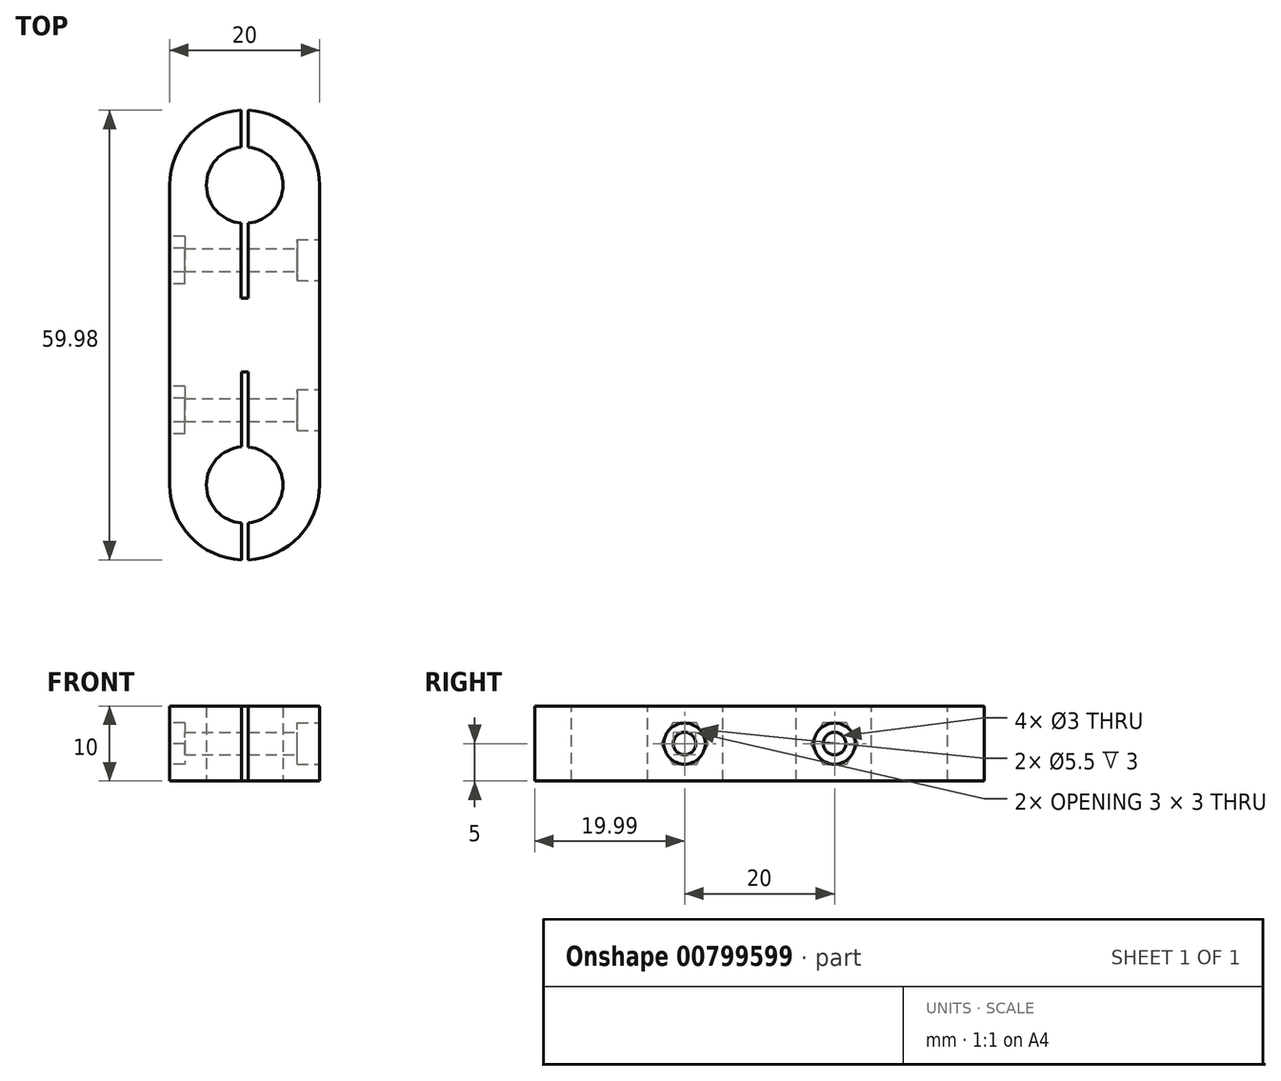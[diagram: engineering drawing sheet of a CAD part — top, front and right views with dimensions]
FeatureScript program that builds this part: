
annotation { "Feature Type Name" : "Feature", "Feature Type Description" : "" }
export const myFeature = defineFeature(function(context is Context, id is Id, definition is map)
    precondition{}
    {
        {
            var Q0;
            Q0=qCreatedBy(makeId("Top.planeOp"),FACE);
            var sketch = newSketch(context, id + "F0", { "sketchPlane" : qUnion([Q0])});
            skCircle(sketch, "E0", {"center": v(0, 0) * mm, "radius": 5.1 * mm});
            skCircle(sketch, "E1", {"center": v(0, 0) * mm, "radius": 10 * mm});
            skPoint(sketch, "E2", {"position": v(0, -40) * mm});
            skCircle(sketch, "E3", {"center": v(0, -40) * mm, "radius": 5.1 * mm});
            skCircle(sketch, "E4", {"center": v(0, -40) * mm, "radius": 10 * mm});
            skLineSegment(sketch, "E5", {"start": v(10, 0) * mm, "end": v(10, -40) * mm});
            skLineSegment(sketch, "E6", {"start": v(-10, 0) * mm, "end": v(-10, -40) * mm});
            skSolve(sketch);
        }
        {
            var Q0;
            Q0=makeQuery(id+"F0.imprint","IMPRINT",FACE,{"disambiguationData":[TD([[makeQuery(id+"F0.imprint","IMPRINT",EDGE,{"derivedFrom":sQuery(id+"F0.wireOp",EDGE,"E0")}),-1.0]])]});
            var Q1;
            {var subQ0=sQuery(id+"F0.wireOp",EDGE,"E5");Q1=makeQuery(id+"F0.imprint","IMPRINT",FACE,{"disambiguationData":[TD([[makeQuery(id+"F0.imprint","IMPRINT",EDGE,{"derivedFrom":subQ0}),-1.0]])]});}
            var Q2;
            Q2=makeQuery(id+"F0.imprint","IMPRINT",FACE,{"disambiguationData":[TD([[makeQuery(id+"F0.imprint","IMPRINT",EDGE,{"derivedFrom":sQuery(id+"F0.wireOp",EDGE,"E3")}),-1.0]])]});
            extrude(context, id + "F1", {"entities" : qUnion([Q0, Q1, Q2]), "depth" : 10 * mm, "offsetDistance" : 25 * mm});
        }
        {
            var Q0;
            Q0=makeQuery(id+"F1.opExtrude","SWEPT_FACE",FACE,{"disambiguationData":[OSD([sQuery(id+"F0.wireOp",EDGE,"E5")])]});
            var sketch = newSketch(context, id + "F2", { "sketchPlane" : qUnion([Q0])});
            skPoint(sketch, "E7", {"position": v(-30, 5) * mm});
            skPoint(sketch, "E8", {"position": v(-10, 5) * mm});
            skCircle(sketch, "E9", {"center": v(-30, 5) * mm, "radius": 1.5 * mm});
            skCircle(sketch, "E10", {"center": v(-10, 5) * mm, "radius": 1.5 * mm});
            skSolve(sketch);
        }
        {
            var Q0;
            Q0=makeQuery(id+"F2.imprint","IMPRINT",FACE,{"disambiguationData":[TD([[makeQuery(id+"F2.imprint","IMPRINT",EDGE,{"derivedFrom":sQuery(id+"F2.wireOp",EDGE,"E9")}),1.0]])]});
            var Q1;
            Q1=makeQuery(id+"F2.imprint","IMPRINT",FACE,{"disambiguationData":[TD([[makeQuery(id+"F2.imprint","IMPRINT",EDGE,{"derivedFrom":sQuery(id+"F2.wireOp",EDGE,"E10")}),1.0]])]});
            extrude(context, id + "F3", {"entities" : qUnion([Q0, Q1]), "operationType" : NewBodyOperationType.REMOVE, "oppositeDirection" : true, "depth" : 25 * mm, "offsetDistance" : 25 * mm});
        }
        {
            var Q0;
            Q0=makeQuery(id+"F1.opExtrude","CAP_FACE",FACE,{"disambiguationData":[OSD([sQuery(id+"F0.wireOp",EDGE,"E0"),sQuery(id+"F0.wireOp",EDGE,"E1"),sQuery(id+"F0.wireOp",EDGE,"E3"),sQuery(id+"F0.wireOp",EDGE,"E4"),sQuery(id+"F0.wireOp",EDGE,"E5"),sQuery(id+"F0.wireOp",EDGE,"E6")])],"isStart":false});
            var sketch = newSketch(context, id + "F4", { "sketchPlane" : qUnion([Q0])});
            skLineSegment(sketch, "E11.bottom", {"start": v(-0.5, 14.81) * mm, "end": v(0.5, 14.81) * mm});
            skLineSegment(sketch, "E11.top", {"start": v(-0.5, -15.1) * mm, "end": v(0.5, -15.1) * mm});
            skLineSegment(sketch, "E11.left", {"start": v(-0.5, 14.81) * mm, "end": v(-0.5, -15.1) * mm});
            skLineSegment(sketch, "E11.right", {"start": v(0.5, 14.81) * mm, "end": v(0.5, -15.1) * mm});
            skLineSegment(sketch, "E12.bottom", {"start": v(-0.44, -24.9) * mm, "end": v(0.5, -24.9) * mm});
            skLineSegment(sketch, "E12.top", {"start": v(-0.44, -52.97) * mm, "end": v(0.5, -52.97) * mm});
            skLineSegment(sketch, "E12.left", {"start": v(-0.44, -24.9) * mm, "end": v(-0.44, -52.97) * mm});
            skLineSegment(sketch, "E12.right", {"start": v(0.5, -24.9) * mm, "end": v(0.5, -52.97) * mm});
            skSolve(sketch);
        }
        {
            var Q0;
            {var subQ0=sQuery(id+"F4.wireOp",EDGE,"E12.bottom");Q0=makeQuery(id+"F4.imprint","IMPRINT",FACE,{"disambiguationData":[TD([[makeQuery(id+"F4.imprint","IMPRINT",EDGE,{"derivedFrom":subQ0}),-1.0]])]});}
            var Q1;
            {var subQ0=sQuery(id+"F4.wireOp",EDGE,"E12.left");var subQ1=makeQuery(id+"F1.opExtrude","CAP_EDGE",EDGE,{"disambiguationData":[OSD([sQuery(id+"F0.wireOp",EDGE,"E4")])],"isStart":false});var subQ2=makeQuery(id+"F4.imprint","INTERSECT",VERTEX,{"derivedFrom":[subQ1,subQ0]});Q1=makeQuery(id+"F4.imprint","IMPRINT",FACE,{"disambiguationData":[TD([[makeQuery(id+"F4.imprint","IMPRINT",EDGE,{"disambiguationData":[TD([[subQ2,1.0]])],"derivedFrom":subQ0}),1.0]])]});}
            var Q2;
            {var subQ0=sQuery(id+"F4.wireOp",EDGE,"E11.top");Q2=makeQuery(id+"F4.imprint","IMPRINT",FACE,{"disambiguationData":[TD([[makeQuery(id+"F4.imprint","IMPRINT",EDGE,{"derivedFrom":subQ0}),1.0]])]});}
            var Q3;
            {var subQ0=sQuery(id+"F4.wireOp",EDGE,"E11.left");var subQ1=makeQuery(id+"F1.opExtrude","CAP_EDGE",EDGE,{"disambiguationData":[OSD([sQuery(id+"F0.wireOp",EDGE,"E1")])],"isStart":false});var subQ2=makeQuery(id+"F4.imprint","INTERSECT",VERTEX,{"derivedFrom":[subQ1,subQ0]});Q3=makeQuery(id+"F4.imprint","IMPRINT",FACE,{"disambiguationData":[TD([[makeQuery(id+"F4.imprint","IMPRINT",EDGE,{"disambiguationData":[TD([[subQ2,-1.0]])],"derivedFrom":subQ0}),1.0]])]});}
            extrude(context, id + "F5", {"entities" : qUnion([Q0, Q1, Q2, Q3]), "operationType" : NewBodyOperationType.REMOVE, "oppositeDirection" : true, "depth" : 25 * mm, "offsetDistance" : 25 * mm});
        }
        {
            var Q0;
            Q0=makeQuery(id+"F1.opExtrude","SWEPT_FACE",FACE,{"disambiguationData":[OSD([sQuery(id+"F0.wireOp",EDGE,"E5")])]});
            var sketch = newSketch(context, id + "F6", { "sketchPlane" : qUnion([Q0])});
            skCircle(sketch, "E13", {"center": v(-30, 5) * mm, "radius": 2.75 * mm});
            skCircle(sketch, "E14", {"center": v(-10, 5) * mm, "radius": 2.75 * mm});
            skSolve(sketch);
        }
        {
            var Q0;
            Q0=makeQuery(id+"F6.imprint","IMPRINT",FACE,{"disambiguationData":[TD([[makeQuery(id+"F6.imprint","IMPRINT",EDGE,{"derivedFrom":sQuery(id+"F6.wireOp",EDGE,"E13")}),1.0]])]});
            var Q1;
            Q1=makeQuery(id+"F6.imprint","IMPRINT",FACE,{"disambiguationData":[TD([[makeQuery(id+"F6.imprint","IMPRINT",EDGE,{"derivedFrom":sQuery(id+"F6.wireOp",EDGE,"E14")}),1.0]])]});
            extrude(context, id + "F7", {"entities" : qUnion([Q0, Q1]), "operationType" : NewBodyOperationType.REMOVE, "oppositeDirection" : true, "depth" : 3 * mm, "offsetDistance" : 25 * mm});
        }
        {
            var Q0;
            Q0=makeQuery(id+"F1.opExtrude","SWEPT_FACE",FACE,{"disambiguationData":[OSD([sQuery(id+"F0.wireOp",EDGE,"E6")])]});
            var sketch = newSketch(context, id + "F8", { "sketchPlane" : qUnion([Q0])});
            skCircle(sketch, "E15.cCircle", {"center": v(10, 5) * mm, "radius": 2.75 * mm, "construction": true});
            skLineSegment(sketch, "E15.0", {"start": v(11.59, 2.25) * mm, "end": v(8.41, 2.25) * mm});
            skLineSegment(sketch, "E15.1", {"start": v(8.41, 2.25) * mm, "end": v(6.82, 5) * mm});
            skLineSegment(sketch, "E15.2", {"start": v(6.82, 5) * mm, "end": v(8.41, 7.75) * mm});
            skLineSegment(sketch, "E15.3", {"start": v(8.41, 7.75) * mm, "end": v(11.59, 7.75) * mm});
            skLineSegment(sketch, "E15.4", {"start": v(11.59, 7.75) * mm, "end": v(13.18, 5) * mm});
            skLineSegment(sketch, "E15.5", {"start": v(13.18, 5) * mm, "end": v(11.59, 2.25) * mm});
            skPoint(sketch, "E15.0.midPoint", {"position": v(10, 2.25) * mm});
            skCircle(sketch, "E16.cCircle", {"center": v(30, 5) * mm, "radius": 2.75 * mm, "construction": true});
            skLineSegment(sketch, "E16.0", {"start": v(31.59, 2.25) * mm, "end": v(28.41, 2.25) * mm});
            skLineSegment(sketch, "E16.1", {"start": v(28.41, 2.25) * mm, "end": v(26.82, 5) * mm});
            skLineSegment(sketch, "E16.2", {"start": v(26.82, 5) * mm, "end": v(28.41, 7.75) * mm});
            skLineSegment(sketch, "E16.3", {"start": v(28.41, 7.75) * mm, "end": v(31.59, 7.75) * mm});
            skLineSegment(sketch, "E16.4", {"start": v(31.59, 7.75) * mm, "end": v(33.18, 5) * mm});
            skLineSegment(sketch, "E16.5", {"start": v(33.18, 5) * mm, "end": v(31.59, 2.25) * mm});
            skPoint(sketch, "E16.0.midPoint", {"position": v(30, 2.25) * mm});
            skSolve(sketch);
        }
        {
            var Q0;
            Q0=makeQuery(id+"F8.imprint","IMPRINT",FACE,{"disambiguationData":[TD([[makeQuery(id+"F8.imprint","IMPRINT",EDGE,{"derivedFrom":sQuery(id+"F8.wireOp",EDGE,"E15.0")}),-1.0]])]});
            var Q1;
            Q1=makeQuery(id+"F8.imprint","IMPRINT",FACE,{"disambiguationData":[TD([[makeQuery(id+"F8.imprint","IMPRINT",EDGE,{"derivedFrom":sQuery(id+"F8.wireOp",EDGE,"E16.0")}),-1.0]])]});
            extrude(context, id + "F9", {"entities" : qUnion([Q0, Q1]), "operationType" : NewBodyOperationType.REMOVE, "oppositeDirection" : true, "depth" : 2 * mm, "offsetDistance" : 25 * mm});
        }
    });
